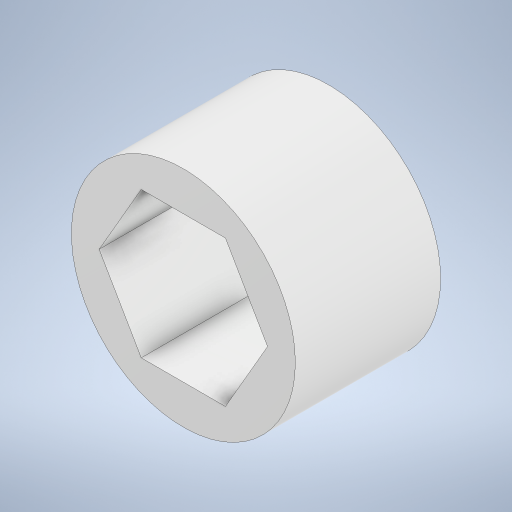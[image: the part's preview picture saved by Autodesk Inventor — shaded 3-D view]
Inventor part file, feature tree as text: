
AUTODESK INVENTOR PART (.ipt)
format: ipt  version: 2024 (Build 280153000, 153)  size: 225,280 bytes
history: native  units: in
note: dims shown in document units (in); Inventor stores cm internally (conversion verified against a paired STEP export)
features: extrude x1, sketch x1
ambient origin geometry x8: Origin, YZ Plane, XZ Plane, XY Plane, X Axis, Y Axis, Z Axis, Center Point
bodies: Solid1 (feature_tree)
feature tree (2):
  extrude  "Extrusion1"  Depth=0.5in
  sketch  "Sketch1"  dims[d0=0.7677in d1=0.5in d2=0.498in d3=0.0in]
